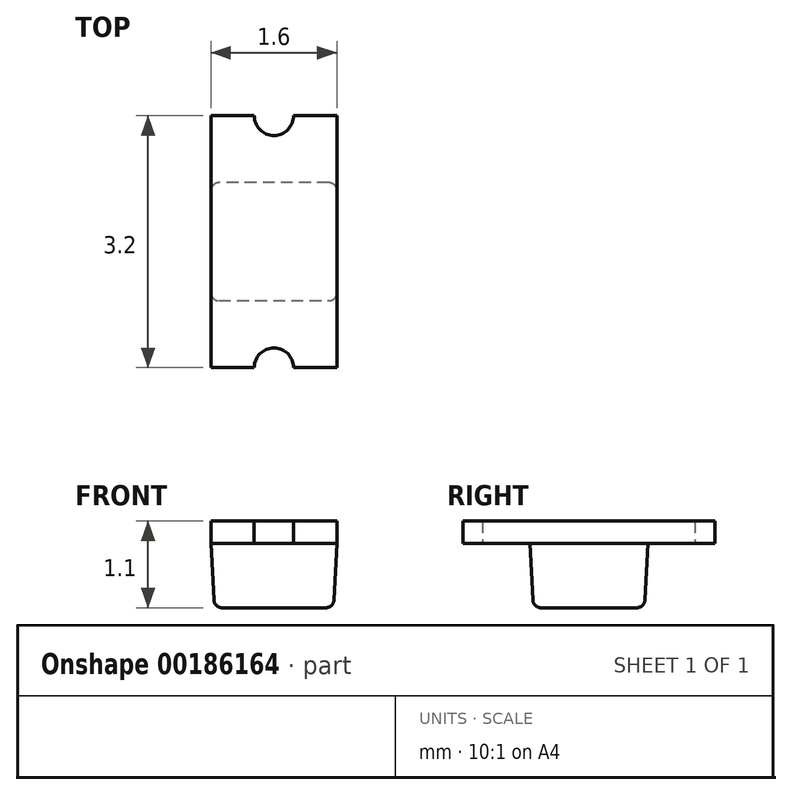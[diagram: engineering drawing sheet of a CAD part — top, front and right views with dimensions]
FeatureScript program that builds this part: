
annotation { "Feature Type Name" : "Feature", "Feature Type Description" : "" }
export const myFeature = defineFeature(function(context is Context, id is Id, definition is map)
    precondition{}
    {
        {
            var Q0;
            Q0=qCreatedBy(makeId("Top.planeOp"),FACE);
            var sketch = newSketch(context, id + "F0", { "sketchPlane" : qUnion([Q0])});
            skLineSegment(sketch, "E0.bottom", {"start": v(0.8, -1.6) * mm, "end": v(0.25, -1.6) * mm});
            skLineSegment(sketch, "E0.top", {"start": v(0.8, 1.6) * mm, "end": v(0.25, 1.6) * mm});
            skLineSegment(sketch, "E0.left", {"start": v(0.8, -1.6) * mm, "end": v(0.8, 1.6) * mm});
            skLineSegment(sketch, "E0.right", {"start": v(-0.8, -1.6) * mm, "end": v(-0.8, 1.6) * mm});
            skPoint(sketch, "E0.middle", {"position": v(0, 0) * mm});
            skArc(sketch, "E1", {"start": v(-0.25, 1.6) * mm, "mid": v(0, 1.35) * mm, "end": v(0.25, 1.6) * mm});
            skLineSegment(sketch, "E2.trimOffspring", {"start": v(-0.25, 1.6) * mm, "end": v(-0.8, 1.6) * mm});
            skLineSegment(sketch, "E3", {"start": v(0, 0) * mm, "end": v(0.8, 0) * mm, "construction": true});
            skArc(sketch, "E4.MirrorCS", {"start": v(-0.25, -1.6) * mm, "mid": v(0, -1.35) * mm, "end": v(0.25, -1.6) * mm});
            skLineSegment(sketch, "E5.trimOffspring", {"start": v(-0.25, -1.6) * mm, "end": v(-0.8, -1.6) * mm});
            skSolve(sketch);
        }
        {
            var Q0;
            Q0 = qSketchRegion(id + "F0", true);
            extrude(context, id + "F1", {"entities" : qUnion([Q0]), "depth" : .28 * mm});
        }
        {
            var Q0;
            Q0=makeQuery(id+"F1.opExtrude","CAP_FACE",FACE,{"disambiguationData":[OSD([sQuery(id+"F0.wireOp",EDGE,"E0.bottom"),sQuery(id+"F0.wireOp",EDGE,"E0.top"),sQuery(id+"F0.wireOp",EDGE,"E0.left"),sQuery(id+"F0.wireOp",EDGE,"E0.right"),sQuery(id+"F0.wireOp",EDGE,"E1"),sQuery(id+"F0.wireOp",EDGE,"E2.trimOffspring"),sQuery(id+"F0.wireOp",EDGE,"E4.MirrorCS"),sQuery(id+"F0.wireOp",EDGE,"E5.trimOffspring")])],"isStart":true});
            var sketch = newSketch(context, id + "F2", { "sketchPlane" : qUnion([Q0])});
            skLineSegment(sketch, "E6.bottom", {"start": v(-0.8, -0.75) * mm, "end": v(0.8, -0.75) * mm});
            skLineSegment(sketch, "E6.top", {"start": v(-0.8, 0.75) * mm, "end": v(0.8, 0.75) * mm});
            skLineSegment(sketch, "E6.left", {"start": v(-0.8, -0.75) * mm, "end": v(-0.8, 0.75) * mm});
            skLineSegment(sketch, "E6.right", {"start": v(0.8, -0.75) * mm, "end": v(0.8, 0.75) * mm});
            skPoint(sketch, "E6.middle", {"position": v(0, 0) * mm});
            skSolve(sketch);
        }
        {
            var Q0;
            Q0 = qSketchRegion(id + "F2", true);
            extrude(context, id + "F3", {"entities" : qUnion([Q0]), "operationType" : NewBodyOperationType.ADD, "depth" : 1.1 * mm - 0.28 * mm, "hasDraft" : true, "draftAngle" : 3 * degree, "draftPullDirection" : true});
        }
        {
            var Q0;
            Q0=makeQuery(id+"F3.opExtrude","CAP_FACE",FACE,{"disambiguationData":[OSD([sQuery(id+"F2.wireOp",EDGE,"E6.bottom"),sQuery(id+"F2.wireOp",EDGE,"E6.top"),sQuery(id+"F2.wireOp",EDGE,"E6.left"),sQuery(id+"F2.wireOp",EDGE,"E6.right")])],"isStart":false});
            var Q1;
            Q1=makeQuery(id+"F3.opExtrude","SWEPT_EDGE",EDGE,{"disambiguationData":[OSD([sQuery(id+"F0.wireOp",EDGE,"E0.left"),sQuery(id+"F2.wireOp",EDGE,"E6.bottom"),sQuery(id+"F2.wireOp",EDGE,"E6.right")])]});
            var Q2;
            Q2=makeQuery(id+"F3.opExtrude","SWEPT_EDGE",EDGE,{"disambiguationData":[OSD([sQuery(id+"F0.wireOp",EDGE,"E0.left"),sQuery(id+"F2.wireOp",EDGE,"E6.top"),sQuery(id+"F2.wireOp",EDGE,"E6.right")])]});
            var Q3;
            Q3=makeQuery(id+"F3.opExtrude","SWEPT_EDGE",EDGE,{"disambiguationData":[OSD([sQuery(id+"F0.wireOp",EDGE,"E0.right"),sQuery(id+"F2.wireOp",EDGE,"E6.top"),sQuery(id+"F2.wireOp",EDGE,"E6.left")])]});
            var Q4;
            Q4=makeQuery(id+"F3.opExtrude","SWEPT_EDGE",EDGE,{"disambiguationData":[OSD([sQuery(id+"F0.wireOp",EDGE,"E0.right"),sQuery(id+"F2.wireOp",EDGE,"E6.bottom"),sQuery(id+"F2.wireOp",EDGE,"E6.left")])]});
            fillet(context, id + "F4", {"entities" : qUnion([Q0, Q1, Q2, Q3, Q4]), "radius" : 0.1 * mm, "tangentPropagation" : true, "allowEdgeOverflow" : false});
        }
    });
